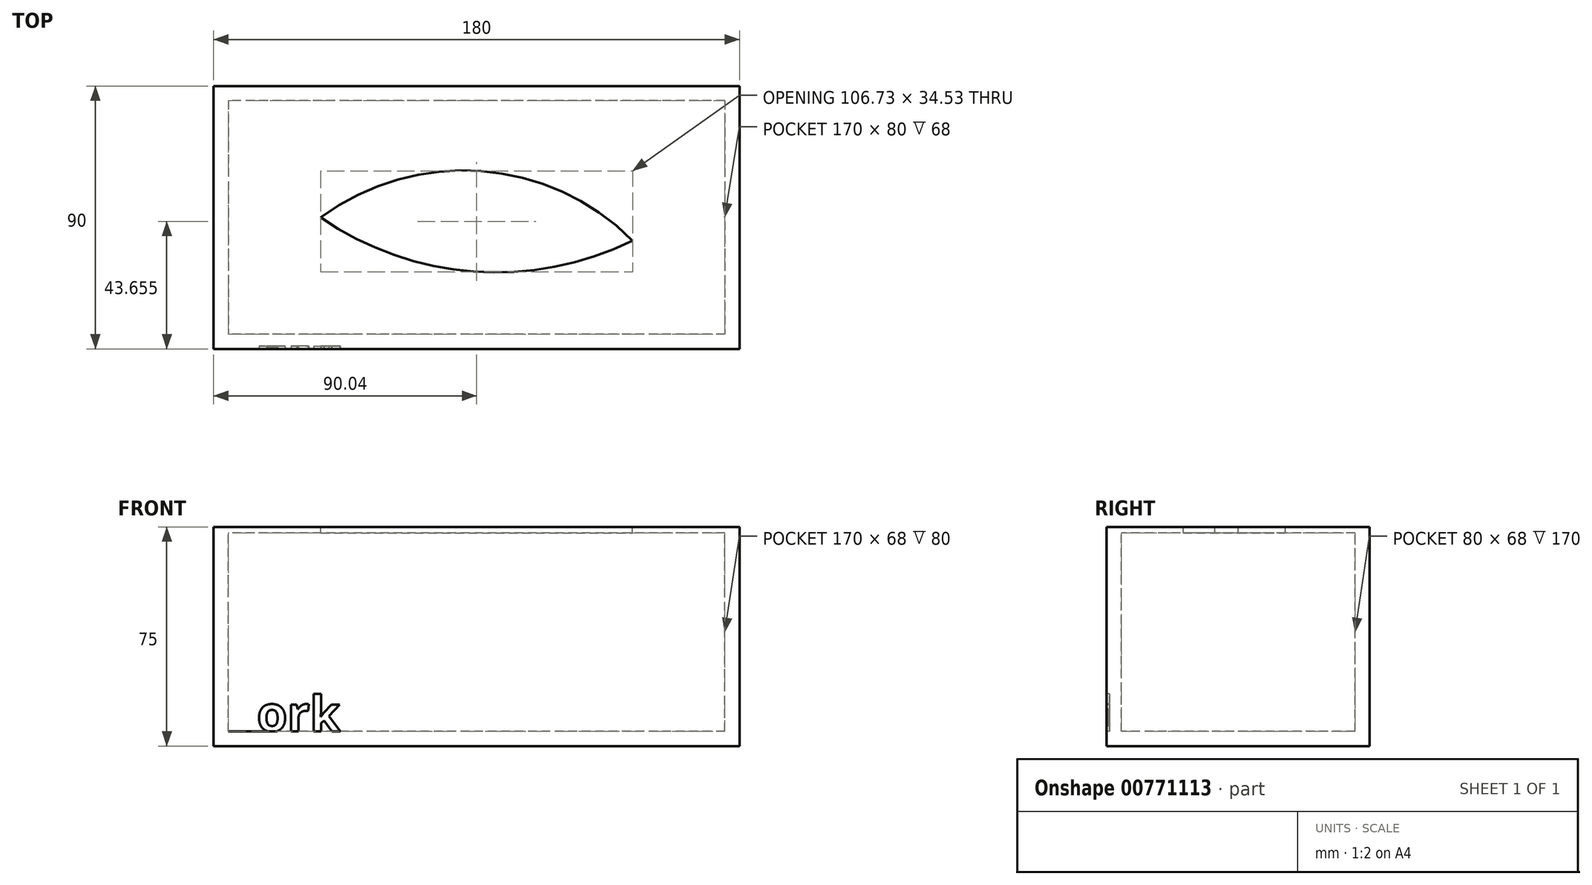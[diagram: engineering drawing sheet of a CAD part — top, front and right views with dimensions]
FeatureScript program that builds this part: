
annotation { "Feature Type Name" : "Feature", "Feature Type Description" : "" }
export const myFeature = defineFeature(function(context is Context, id is Id, definition is map)
    precondition{}
    {
        {
            var Q0;
            Q0=qCreatedBy(makeId("Top.planeOp"),FACE);
            var sketch = newSketch(context, id + "F0", { "sketchPlane" : qUnion([Q0])});
            skLineSegment(sketch, "E0.bottom", {"start": v(90, -45) * mm, "end": v(-90, -45) * mm});
            skLineSegment(sketch, "E0.top", {"start": v(90, 45) * mm, "end": v(-90, 45) * mm});
            skLineSegment(sketch, "E0.left", {"start": v(90, -45) * mm, "end": v(90, 45) * mm});
            skLineSegment(sketch, "E0.right", {"start": v(-90, -45) * mm, "end": v(-90, 45) * mm});
            skPoint(sketch, "E0.middle", {"position": v(0, 0) * mm});
            skSolve(sketch);
        }
        {
            var Q0;
            Q0=makeQuery(id+"F0.imprint","IMPRINT",FACE,{"disambiguationData":[TD([[makeQuery(id+"F0.imprint","IMPRINT",EDGE,{"derivedFrom":sQuery(id+"F0.wireOp",EDGE,"E0.bottom")}),-1.0]])]});
            extrude(context, id + "F1", {"entities" : qUnion([Q0]), "depth" : 75 * mm, "offsetDistance" : 25 * mm});
        }
        {
            var Q0;
            Q0=makeQuery(id+"F1.opExtrude","SWEPT_FACE",FACE,{"disambiguationData":[OSD([sQuery(id+"F0.wireOp",EDGE,"E0.right")])]});
            var sketch = newSketch(context, id + "F2", { "sketchPlane" : qUnion([Q0])});
            skLineSegment(sketch, "E1.bottom", {"start": v(-45, 0) * mm, "end": v(45, 0) * mm});
            skLineSegment(sketch, "E1.top", {"start": v(-45, 75) * mm, "end": v(45, 75) * mm});
            skLineSegment(sketch, "E1.left", {"start": v(-45, 0) * mm, "end": v(-45, 75) * mm});
            skLineSegment(sketch, "E1.right", {"start": v(45, 0) * mm, "end": v(45, 75) * mm});
            skLineSegment(sketch, "E2.0", {"start": v(-45, 73) * mm, "end": v(45, 73) * mm});
            skLineSegment(sketch, "E3.0", {"start": v(-40, 0) * mm, "end": v(-40, 75) * mm});
            skLineSegment(sketch, "E4.0", {"start": v(-45, 5) * mm, "end": v(45, 5) * mm});
            skLineSegment(sketch, "E5.0", {"start": v(40, 0) * mm, "end": v(40, 75) * mm});
            skSolve(sketch);
        }
        {
            var Q0;
            {var subQ0=sQuery(id+"F2.wireOp",EDGE,"E3.0");var subQ1=sQuery(id+"F2.wireOp",EDGE,"E2.0");var subQ2=makeQuery(id+"F2.imprint","INTERSECT",VERTEX,{"derivedFrom":[subQ1,subQ0]});Q0=makeQuery(id+"F2.imprint","IMPRINT",FACE,{"disambiguationData":[TD([[makeQuery(id+"F2.imprint","IMPRINT",EDGE,{"disambiguationData":[TD([[subQ2,-1.0]])],"derivedFrom":subQ1}),-1.0]])]});}
            extrude(context, id + "F3", {"entities" : qUnion([Q0]), "operationType" : NewBodyOperationType.REMOVE, "oppositeDirection" : true, "depth" : 175 * mm, "offsetDistance" : 25 * mm});
        }
        {
            var Q0;
            Q0=makeQuery(id+"F1.opExtrude","SWEPT_FACE",FACE,{"disambiguationData":[OSD([sQuery(id+"F0.wireOp",EDGE,"E0.right")])]});
            var sketch = newSketch(context, id + "F4", { "sketchPlane" : qUnion([Q0])});
            skLineSegment(sketch, "E6.bottom", {"start": v(-40, 5) * mm, "end": v(40, 5) * mm});
            skLineSegment(sketch, "E6.top", {"start": v(-40, 73) * mm, "end": v(40, 73) * mm});
            skLineSegment(sketch, "E6.left", {"start": v(-40, 5) * mm, "end": v(-40, 73) * mm});
            skLineSegment(sketch, "E6.right", {"start": v(40, 5) * mm, "end": v(40, 73) * mm});
            skSolve(sketch);
        }
        {
            var Q0;
            Q0=makeQuery(id+"F4.imprint","IMPRINT",FACE,{"disambiguationData":[TD([[makeQuery(id+"F4.imprint","IMPRINT",EDGE,{"derivedFrom":sQuery(id+"F4.wireOp",EDGE,"E6.bottom")}),1.0]])]});
            extrude(context, id + "F5", {"entities" : qUnion([Q0]), "operationType" : NewBodyOperationType.ADD, "oppositeDirection" : true, "depth" : 5 * mm, "offsetDistance" : 25 * mm});
        }
        {
            var Q0;
            Q0=makeQuery(id+"F1.opExtrude","CAP_FACE",FACE,{"disambiguationData":[OSD([sQuery(id+"F0.wireOp",EDGE,"E0.bottom"),sQuery(id+"F0.wireOp",EDGE,"E0.top"),sQuery(id+"F0.wireOp",EDGE,"E0.left"),sQuery(id+"F0.wireOp",EDGE,"E0.right")])],"isStart":false});
            var sketch = newSketch(context, id + "F6", { "sketchPlane" : qUnion([Q0])});
            skArc(sketch, "E7", {"start": v(-53.32, 0) * mm, "mid": v(-1.04, -18.5) * mm, "end": v(53.4, -7.9) * mm});
            skArc(sketch, "E8", {"start": v(53.4, -7.9) * mm, "mid": v(1.51, 15.92) * mm, "end": v(-53.32, 0) * mm});
            skSolve(sketch);
        }
        {
            var Q0;
            Q0=makeQuery(id+"F6.imprint","IMPRINT",FACE,{"disambiguationData":[TD([[makeQuery(id+"F6.imprint","IMPRINT",EDGE,{"derivedFrom":sQuery(id+"F6.wireOp",EDGE,"E7")}),1.0]])]});
            extrude(context, id + "F7", {"entities" : qUnion([Q0]), "operationType" : NewBodyOperationType.REMOVE, "endBound" : BoundingType.SYMMETRIC, "oppositeDirection" : true, "depth" : 50 * mm, "offsetDistance" : 25 * mm});
        }
        {
            var Q0;
            Q0=makeQuery(id+"F1.opExtrude","SWEPT_FACE",FACE,{"disambiguationData":[OSD([sQuery(id+"F0.wireOp",EDGE,"E0.bottom")])]});
            var sketch = newSketch(context, id + "F8", { "sketchPlane" : qUnion([Q0])});
            skLineSegment(sketch, "E9.0", {"start": v(90, 5) * mm, "end": v(-90, 5) * mm});
            skLineSegment(sketch, "E10.0", {"start": v(-85, 75) * mm, "end": v(-85, 0) * mm});
            skText(sketch, "E11", { "text": "Tork\n", "fontName": "OpenSans-Bold.ttf"});
            const initialGuessF8  = {"E11": [-0.085, 0.005, 1, 0, 0.01216]};
            skSetInitialGuess(sketch, initialGuessF8);
            skSolve(sketch);
        }
        {
            var Q0;
            Q0=makeQuery(id+"F8.imprint","IMPRINT",FACE,{"disambiguationData":[TD([[makeQuery(id+"F8.imprint","IMPRINT",EDGE,{"derivedFrom":sQuery(id+"F8.wireOp",EDGE,"E11.sketch_text.stroke-0")}),-1.0]])]});
            var Q1;
            Q1=makeQuery(id+"F8.imprint","IMPRINT",FACE,{"disambiguationData":[TD([[makeQuery(id+"F8.imprint","IMPRINT",EDGE,{"derivedFrom":sQuery(id+"F8.wireOp",EDGE,"E11.sketch_text.stroke-8")}),-1.0]])]});
            var Q2;
            Q2=makeQuery(id+"F8.imprint","IMPRINT",FACE,{"disambiguationData":[TD([[makeQuery(id+"F8.imprint","IMPRINT",EDGE,{"derivedFrom":sQuery(id+"F8.wireOp",EDGE,"E11.sketch_text.stroke-26")}),-1.0]])]});
            var Q3;
            Q3=makeQuery(id+"F8.imprint","IMPRINT",FACE,{"disambiguationData":[TD([[makeQuery(id+"F8.imprint","IMPRINT",EDGE,{"derivedFrom":sQuery(id+"F8.wireOp",EDGE,"E11.sketch_text.stroke-39")}),-1.0]])]});
            extrude(context, id + "F9", {"entities" : qUnion([Q0, Q1, Q2, Q3]), "operationType" : NewBodyOperationType.REMOVE, "oppositeDirection" : true, "depth" : 1 * mm, "offsetDistance" : 25 * mm});
        }
        {
            var Q0;
            Q0=makeQuery(id+"F9.boolean.opBoolean","SPLIT",FACE,{"disambiguationData":[TD([makeQuery(id+"F9.opExtrude","SWEPT_FACE",FACE,{"disambiguationData":[OSD([sQuery(id+"F8.wireOp",EDGE,"E11.sketch_text.stroke-8")])]})])],"derivedFrom":makeQuery(id+"F1.opExtrude","SWEPT_FACE",FACE,{"disambiguationData":[OSD([sQuery(id+"F0.wireOp",EDGE,"E0.bottom")])]})});
            extrude(context, id + "F10", {"entities" : qUnion([Q0]), "operationType" : NewBodyOperationType.REMOVE, "oppositeDirection" : true, "depth" : .5 * mm, "offsetDistance" : 25 * mm});
        }
    });
